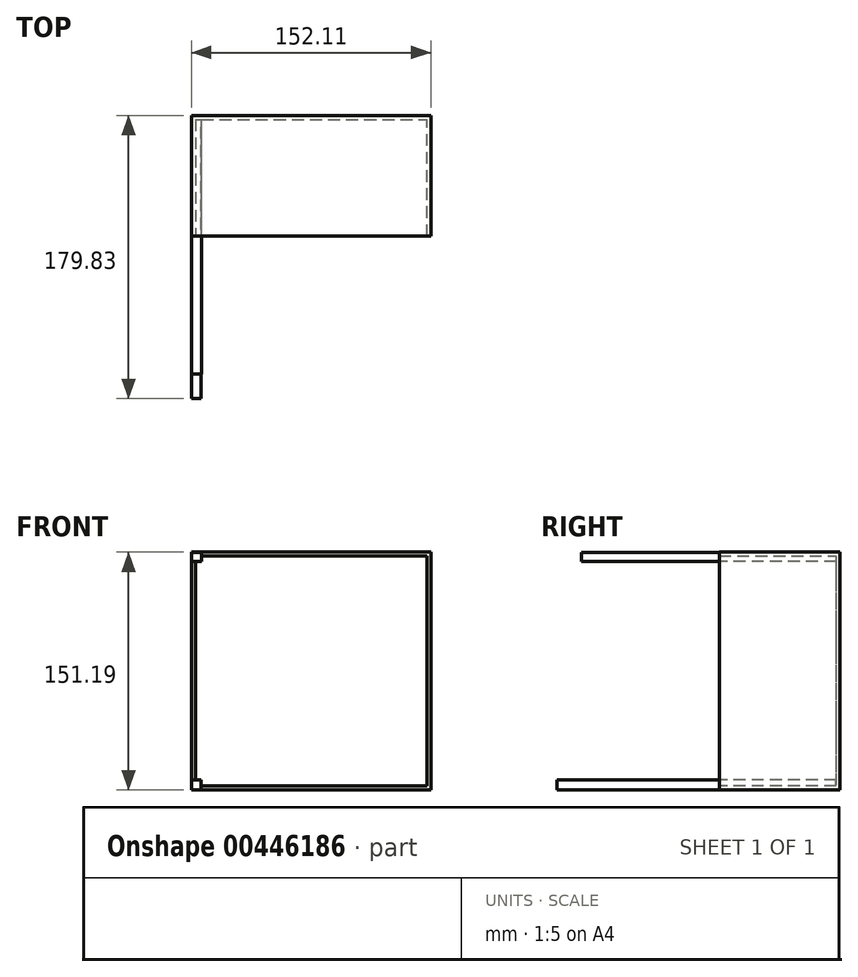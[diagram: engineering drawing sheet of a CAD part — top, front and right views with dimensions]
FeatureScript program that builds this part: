
annotation { "Feature Type Name" : "Feature", "Feature Type Description" : "" }
export const myFeature = defineFeature(function(context is Context, id is Id, definition is map)
    precondition{}
    {
        {
            var Q0;
            Q0=qCreatedBy(makeId("Front.planeOp"),FACE);
            var sketch = newSketch(context, id + "F0", { "sketchPlane" : qUnion([Q0])});
            skLineSegment(sketch, "E0.bottom", {"start": v(-76.29, 76.06) * mm, "end": v(75.82, 76.06) * mm});
            skLineSegment(sketch, "E0.top", {"start": v(-76.29, -75.13) * mm, "end": v(75.82, -75.13) * mm});
            skLineSegment(sketch, "E0.left", {"start": v(-76.29, 76.06) * mm, "end": v(-76.29, -75.13) * mm});
            skLineSegment(sketch, "E0.right", {"start": v(75.82, 76.06) * mm, "end": v(75.82, -75.13) * mm});
            skSolve(sketch);
        }
        {
            var Q0;
            Q0=makeQuery(id+"F0.imprint","IMPRINT",FACE,{"disambiguationData":[TD([[makeQuery(id+"F0.imprint","IMPRINT",EDGE,{"derivedFrom":sQuery(id+"F0.wireOp",EDGE,"E0.bottom")}),-1.0]])]});
            extrude(context, id + "F1", {"entities" : qUnion([Q0]), "depth" : 76.7 * mm});
        }
        {
            var Q0;
            Q0=makeQuery(id+"F1.opExtrude","CAP_FACE",FACE,{"disambiguationData":[OSD([sQuery(id+"F0.wireOp",EDGE,"E0.bottom"),sQuery(id+"F0.wireOp",EDGE,"E0.top"),sQuery(id+"F0.wireOp",EDGE,"E0.left"),sQuery(id+"F0.wireOp",EDGE,"E0.right")])],"isStart":false});
            shell(context, id + "F2", {"entities" : qUnion([Q0]), "thickness" : 2.54 * mm});
        }
        {
            var Q0;
            Q0=makeQuery(id+"F2.opShell","OFFSET_FACE",FACE,{"disambiguationData":[OSD([sQuery(id+"F0.wireOp",EDGE,"E0.bottom"),sQuery(id+"F0.wireOp",EDGE,"E0.top"),sQuery(id+"F0.wireOp",EDGE,"E0.left"),sQuery(id+"F0.wireOp",EDGE,"E0.right")])]});
            var sketch = newSketch(context, id + "F3", { "sketchPlane" : qUnion([Q0])});
            skLineSegment(sketch, "E1.bottom", {"start": v(-76.1, 75.82) * mm, "end": v(-69.82, 75.82) * mm});
            skLineSegment(sketch, "E1.top", {"start": v(-76.1, 70) * mm, "end": v(-69.82, 70) * mm});
            skLineSegment(sketch, "E1.left", {"start": v(-76.1, 75.82) * mm, "end": v(-76.1, 70) * mm});
            skLineSegment(sketch, "E1.right", {"start": v(-69.82, 75.82) * mm, "end": v(-69.82, 70) * mm});
            skSolve(sketch);
        }
        {
            var Q0;
            Q0 = qSketchRegion(id + "F3", true);
            extrude(context, id + "F4", {"entities" : qUnion([Q0]), "operationType" : NewBodyOperationType.ADD, "depth" : 161.8 * mm});
        }
        {
            var Q0;
            Q0=makeQuery(id+"F2.opShell","OFFSET_FACE",FACE,{"disambiguationData":[OSD([sQuery(id+"F0.wireOp",EDGE,"E0.bottom"),sQuery(id+"F0.wireOp",EDGE,"E0.top"),sQuery(id+"F0.wireOp",EDGE,"E0.left"),sQuery(id+"F0.wireOp",EDGE,"E0.right")])]});
            var sketch = newSketch(context, id + "F5", { "sketchPlane" : qUnion([Q0])});
            skLineSegment(sketch, "E2.bottom", {"start": v(-76.1, -75.13) * mm, "end": v(-70.05, -75.13) * mm});
            skLineSegment(sketch, "E2.top", {"start": v(-76.1, -68.61) * mm, "end": v(-70.05, -68.61) * mm});
            skLineSegment(sketch, "E2.left", {"start": v(-76.1, -75.13) * mm, "end": v(-76.1, -68.61) * mm});
            skLineSegment(sketch, "E2.right", {"start": v(-70.05, -75.13) * mm, "end": v(-70.05, -68.61) * mm});
            skSolve(sketch);
        }
        {
            var Q0;
            {var subQ12=makeQuery(id+"F4.opExtrude","CAP_EDGE",EDGE,{"disambiguationData":[OSD([sQuery(id+"F3.wireOp",EDGE,"E1.top")])],"isStart":true});Q0=makeQuery(id+"F5.imprint","IMPRINT",FACE,{"disambiguationData":[TD([[makeQuery(id+"F5.imprint","IMPRINT",EDGE,{"derivedFrom":subQ12}),-1.0]])]});}
            var sketch = newSketch(context, id + "F6", { "sketchPlane" : qUnion([Q0])});
            skLineSegment(sketch, "E3.bottom", {"start": v(75.55, -74.2) * mm, "end": v(67.87, -74.2) * mm});
            skLineSegment(sketch, "E3.top", {"start": v(75.55, -67.45) * mm, "end": v(67.87, -67.45) * mm});
            skLineSegment(sketch, "E3.left", {"start": v(75.55, -74.2) * mm, "end": v(75.55, -67.45) * mm});
            skLineSegment(sketch, "E3.right", {"start": v(67.87, -74.2) * mm, "end": v(67.87, -67.45) * mm});
            skSolve(sketch);
        }
        {
            var Q0;
            {var subQ12=makeQuery(id+"F4.opExtrude","CAP_EDGE",EDGE,{"disambiguationData":[OSD([sQuery(id+"F3.wireOp",EDGE,"E1.top")])],"isStart":true});Q0=makeQuery(id+"F5.imprint","IMPRINT",FACE,{"disambiguationData":[TD([[makeQuery(id+"F5.imprint","IMPRINT",EDGE,{"derivedFrom":subQ12}),-1.0]])]});}
            var sketch = newSketch(context, id + "F7", { "sketchPlane" : qUnion([Q0])});
            skLineSegment(sketch, "E4.bottom", {"start": v(75.78, 76.29) * mm, "end": v(67.17, 76.29) * mm});
            skLineSegment(sketch, "E4.top", {"start": v(75.78, 70.94) * mm, "end": v(67.17, 70.94) * mm});
            skLineSegment(sketch, "E4.left", {"start": v(75.78, 76.29) * mm, "end": v(75.78, 70.94) * mm});
            skLineSegment(sketch, "E4.right", {"start": v(67.17, 76.29) * mm, "end": v(67.17, 70.94) * mm});
            skSolve(sketch);
        }
        {
            var Q0;
            Q0 = qSketchRegion(id + "F6", true);
            var Q1;
            Q1 = qSketchRegion(id + "F5", true);
            var Q2;
            Q2 = qSketchRegion(id + "F7", true);
            extrude(context, id + "F8", {"entities" : qUnion([Q0, Q1, Q2]), "operationType" : NewBodyOperationType.ADD, "depth" : 177.3 * mm});
        }
    });
